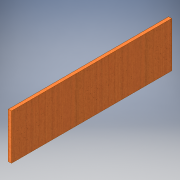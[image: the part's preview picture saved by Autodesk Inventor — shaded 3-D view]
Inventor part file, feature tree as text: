
AUTODESK INVENTOR PART (.ipt)
format: ipt  version: 2016 (Build 200138000, 138)  size: 102,400 bytes
history: native  units: in
note: dims shown in document units (in); Inventor stores cm internally (conversion verified against a paired STEP export)
features: extrude x1, sketch x1
ambient origin geometry x8: Origin, YZ Plane, XZ Plane, XY Plane, X Axis, Y Axis, Z Axis, Center Point
bodies: Solid1 (feature_tree)
feature tree (2):
  extrude  "Extrusion1"  Depth=6.5in
  sketch  "Sketch1"  dims[d0=23.0in d1=6.5in d2=0.4375in d3=0.0in]
